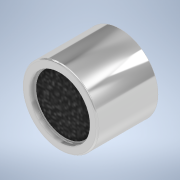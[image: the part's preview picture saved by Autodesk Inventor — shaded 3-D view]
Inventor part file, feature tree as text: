
AUTODESK INVENTOR PART (.ipt)
format: ipt  version: 2021 (Build 250183000, 183)  size: 135,680 bytes
history: native  units: mm
features: extrude x2, sketch x2, other x1, fillet x1
ambient origin geometry x8: Origin, YZ Plane, XZ Plane, XY Plane, X Axis, Y Axis, Z Axis, Center Point
bodies: Body1 (feature_tree)
feature tree (6):
  other  "Sólido1"
  extrude  "Extrusão1"  Depth=12.0mm
  extrude  "Extrusão2"  Depth=11.0mm TaperAngle=0.0deg
  fillet  "Arredondamento1"  Radius=0.3mm
  sketch  "Esboço1"  dims[d0=15.0mm d1=12.0mm]
  sketch  "Esboço2"  dims[d2=12.0mm d3=0.0mm d4=11.0mm d5=0.0mm d6=0.3mm]
